# Revit family: Fireplace_Gas_Heatilator_Legacy
name_source: partatom
category: Mechanical Equipment
revit_build: Autodesk Revit 2015 (Build: 20140606_1530(x64)
units: mm (PartAtom-declared; Revit-internal decimal feet)

## types (2) — shared parameters
Assembly Code = D3020
Construction Details = http://www.arcat.com
Default Elevation = 0' - 0"
Description = Heatilator Gas Burning Fireplace - Legacy as Specified
Door Width = 3' - 8"
DoorHeight = 2' - 6 1/2"
Efficiency Ratings = EnerGuide 19.8
Exhaust Connection Diameter = 9"
Fixture Finish = Metal - HHT - Metallic Black
Fuel Consumption = as Specified
HVAC_BTU Input = 65000.0 Btu/h
HVAC_BTU Output = 0.0 Btu/h
Heating Capacity = as Specified
Keynote = 10305
Manufacturer = Heatilator
Manufacturer Website = http://www.heatilator.com
Model = LEGACY42-IFT
Opening Height = 2' - 4 1/2"
Opening Offset = 0' - 1 7/8"
Opening Width = 3' - 6"
Product Data = http://www.arcat.com
Rear Width = 2' - 10 5/8"
Revision = R1_2018-05
Sales Information = http://www.heatilator.com
Send Message = http://www.arcat.com
Specification = http://www.arcat.com
Standards Conformance = UL 307B  ;  ANSI Z21.50-2016  ;  CSA 2.22-2016
URL = http://www.heatilator.com
Unit Depth = 2' - 4 1/2"
Unit Height = 6' - 2 1/8"
Unit Width = 4' - 2 3/8"
zero-valued in all types: Expected Lifespan (Years), Maintenance Schedule (Months), Unit Weight, Warranty Duration (Years)

## per-type parameters (varying)
| type | Fuel Type |
| 42 x 28.5 Viewing Area NG | Natural Gas |
| 42 x 28.5 Viewing Area LP | Liquid Petroleum |

## geometry (parser evidence)
native form markers: Sweep x6
no freeform markers — native parametric forms only
